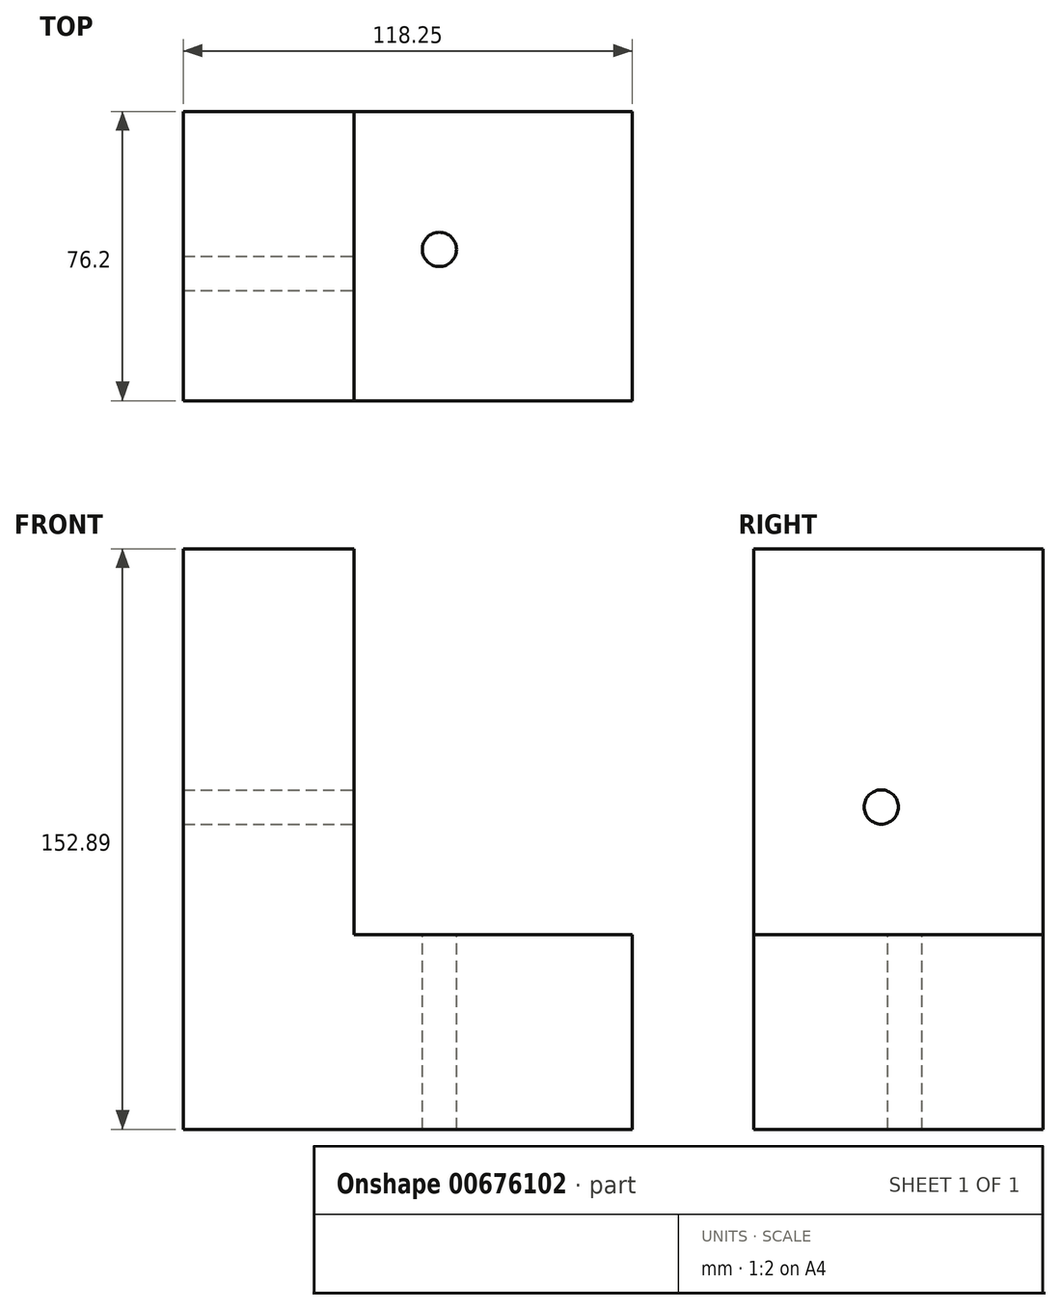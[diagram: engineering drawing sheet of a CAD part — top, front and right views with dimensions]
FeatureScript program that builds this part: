
annotation { "Feature Type Name" : "Feature", "Feature Type Description" : "" }
export const myFeature = defineFeature(function(context is Context, id is Id, definition is map)
    precondition{}
    {
        {
            var Q0;
            Q0=qCreatedBy(makeId("Front.planeOp"),FACE);
            var sketch = newSketch(context, id + "F0", { "sketchPlane" : qUnion([Q0])});
            skLineSegment(sketch, "E0.bottom", {"start": v(-76.14, 76.34) * mm, "end": v(-31.12, 76.34) * mm});
            skLineSegment(sketch, "E0.top", {"start": v(-76.14, -76.34) * mm, "end": v(-31.12, -76.34) * mm});
            skLineSegment(sketch, "E0.left", {"start": v(-76.14, 76.34) * mm, "end": v(-76.14, -76.34) * mm});
            skLineSegment(sketch, "E0.right", {"start": v(-31.12, 76.34) * mm, "end": v(-31.12, -25.3) * mm});
            skLineSegment(sketch, "E1.bottom", {"start": v(-31.12, -25.3) * mm, "end": v(42.11, -25.3) * mm});
            skLineSegment(sketch, "E1.top", {"start": v(-76.14, -76.55) * mm, "end": v(42.11, -76.55) * mm});
            skLineSegment(sketch, "E1.left", {"start": v(-76.14, -25.3) * mm, "end": v(-76.14, -76.55) * mm});
            skLineSegment(sketch, "E1.right", {"start": v(42.11, -25.3) * mm, "end": v(42.11, -76.55) * mm});
            skSolve(sketch);
        }
        {
            var Q0;
            Q0 = qSketchRegion(id + "F0", true);
            extrude(context, id + "F1", {"entities" : qUnion([Q0]), "depth" : 76.2 * mm, "offsetDistance" : 25.4 * mm});
        }
        {
            var Q0;
            Q0=makeQuery(id+"F1.opExtrude","SWEPT_FACE",FACE,{"disambiguationData":[OSD([sQuery(id+"F0.wireOp",EDGE,"E1.bottom")])]});
            var sketch = newSketch(context, id + "F2", { "sketchPlane" : qUnion([Q0])});
            skCircle(sketch, "E2", {"center": v(-8.69, -36.34) * mm, "radius": 4.5 * mm});
            skSolve(sketch);
        }
        {
            var Q0;
            Q0=makeQuery(id+"F1.opExtrude","SWEPT_FACE",FACE,{"disambiguationData":[OSD([sQuery(id+"F0.wireOp",EDGE,"E0.right")])]});
            var sketch = newSketch(context, id + "F3", { "sketchPlane" : qUnion([Q0])});
            skCircle(sketch, "E3", {"center": v(-42.6, 8.34) * mm, "radius": 4.5 * mm});
            skSolve(sketch);
        }
        {
            var Q0;
            Q0 = qSketchRegion(id + "F2", true);
            extrude(context, id + "F4", {"entities" : qUnion([Q0]), "operationType" : NewBodyOperationType.REMOVE, "oppositeDirection" : true, "depth" : 76.2 * mm, "offsetDistance" : 25.4 * mm});
        }
        {
            var Q0;
            Q0 = qSketchRegion(id + "F3", true);
            extrude(context, id + "F5", {"entities" : qUnion([Q0]), "operationType" : NewBodyOperationType.REMOVE, "oppositeDirection" : true, "depth" : 76.2 * mm, "offsetDistance" : 25.4 * mm});
        }
    });
